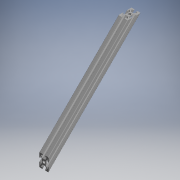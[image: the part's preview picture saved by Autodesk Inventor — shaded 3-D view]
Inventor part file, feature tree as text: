
AUTODESK INVENTOR PART (.ipt)
format: ipt  version: 2017.3 (Build 213256000, 256)  size: 308,736 bytes
history: native  units: mm (DEFAULTED — no unit token found)
features: other x14, sketch x5, extrude x3, revolve x2
ambient origin geometry x8: Origin, YZ Plane, XZ Plane, XY Plane, X Axis, Y Axis, Z Axis, Center Point
bodies: Solid1 (feature_tree)
feature tree (24):
  extrude  "Extrusion1"  Depth=800.0mm TaperAngle=0.0deg
  extrude  "Extrusion2"  TaperAngle=360.0deg  [1 undecoded]
  extrude  "Extrusion3"  TaperAngle=0.0deg  [1 undecoded]
  revolve  "Revolution1"  [1 undecoded]
  revolve  "Revolution2"  [1 undecoded]
  other  "bolt1_XY"
  other  "bolt1_YZ"
  other  "bolt1_ZX"
  other  "bolt1_X"
  other  "bolt1_Y"
  other  "bolt1_Z"
  other  "bolt1_Center"
  other  "bolt2_XY"
  other  "bolt2_YZ"
  other  "bolt2_ZX"
  other  "bolt2_X"
  other  "bolt2_Y"
  other  "bolt2_Z"
  other  "bolt2_Center"
  sketch  "Sketch_1"  dims[d0=284.842712mm d1=0.0mm d2=800.0mm d3=0.0mm]
  sketch  "Sketch_2"  dims[d4=800.0mm d5=0.0mm d6=360.0deg]
  sketch  "Sketch_3"  dims[d7=360.0deg d8=0.0mm d9=0.0mm]
  sketch  "Sketch_4"
  sketch  "Sketch_5"
note: 4 required parameter values undecoded (feature->parameter linkage not recoverable at this tier; creation-order binding heuristic only, values carry confidence <= 0.55)
